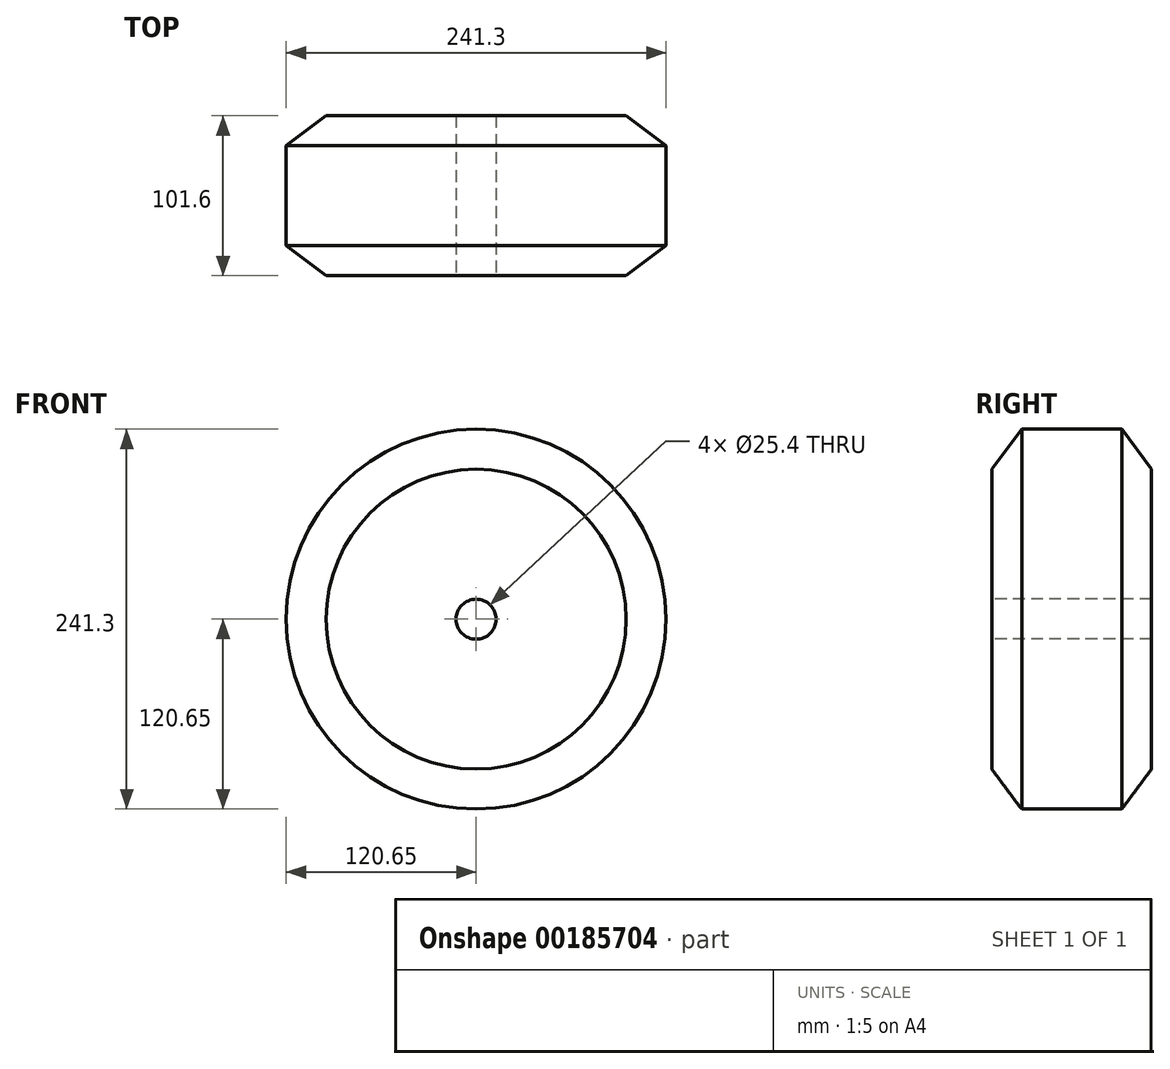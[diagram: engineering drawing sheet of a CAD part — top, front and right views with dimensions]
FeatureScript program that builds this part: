
annotation { "Feature Type Name" : "Feature", "Feature Type Description" : "" }
export const myFeature = defineFeature(function(context is Context, id is Id, definition is map)
    precondition{}
    {
        {
            var Q0;
            Q0=qCreatedBy(makeId("Front.planeOp"),FACE);
            var sketch = newSketch(context, id + "F0", { "sketchPlane" : qUnion([Q0])});
            skCircle(sketch, "E0", {"center": v(0, 0) * mm, "radius": 120.65 * mm});
            skSolve(sketch);
        }
        {
            var Q0;
            Q0=makeQuery(id+"F0.imprint","IMPRINT",FACE,{"disambiguationData":[TD([[makeQuery(id+"F0.imprint","IMPRINT",EDGE,{"derivedFrom":sQuery(id+"F0.wireOp",EDGE,"E0")}),1.0]])]});
            extrude(context, id + "F1", {"entities" : qUnion([Q0]), "depth" : 101.6 * mm});
        }
        {
            var Q0;
            Q0=makeQuery(id+"F1.opExtrude","CAP_EDGE",EDGE,{"disambiguationData":[OSD([sQuery(id+"F0.wireOp",EDGE,"E0")])],"isStart":false});
            var Q1;
            Q1=makeQuery(id+"F1.opExtrude","CAP_EDGE",EDGE,{"disambiguationData":[OSD([sQuery(id+"F0.wireOp",EDGE,"E0")])],"isStart":true});
            chamfer(context, id + "F2", {"entities" : qUnion([Q0, Q1]), "chamferType" : ChamferType.TWO_OFFSETS, "width1" : 25.4 * mm, "oppositeDirection" : false, "width2" : 19.05 * mm, "tangentPropagation" : true});
        }
        {
            var Q0;
            Q0=makeQuery(id+"F1.opExtrude","CAP_FACE",FACE,{"disambiguationData":[OSD([sQuery(id+"F0.wireOp",EDGE,"E0")])],"isStart":false});
            var sketch = newSketch(context, id + "F3", { "sketchPlane" : qUnion([Q0])});
            skCircle(sketch, "E1", {"center": v(0, 0) * mm, "radius": 12.7 * mm});
            skSolve(sketch);
        }
        {
            var Q0;
            Q0=makeQuery(id+"F3.imprint","IMPRINT",FACE,{"disambiguationData":[TD([[makeQuery(id+"F3.imprint","IMPRINT",EDGE,{"derivedFrom":sQuery(id+"F3.wireOp",EDGE,"E1")}),1.0]])]});
            extrude(context, id + "F4", {"entities" : qUnion([Q0]), "operationType" : NewBodyOperationType.REMOVE, "endBound" : BoundingType.UP_TO_NEXT, "oppositeDirection" : true, "depth" : 25.4 * mm});
        }
    });
